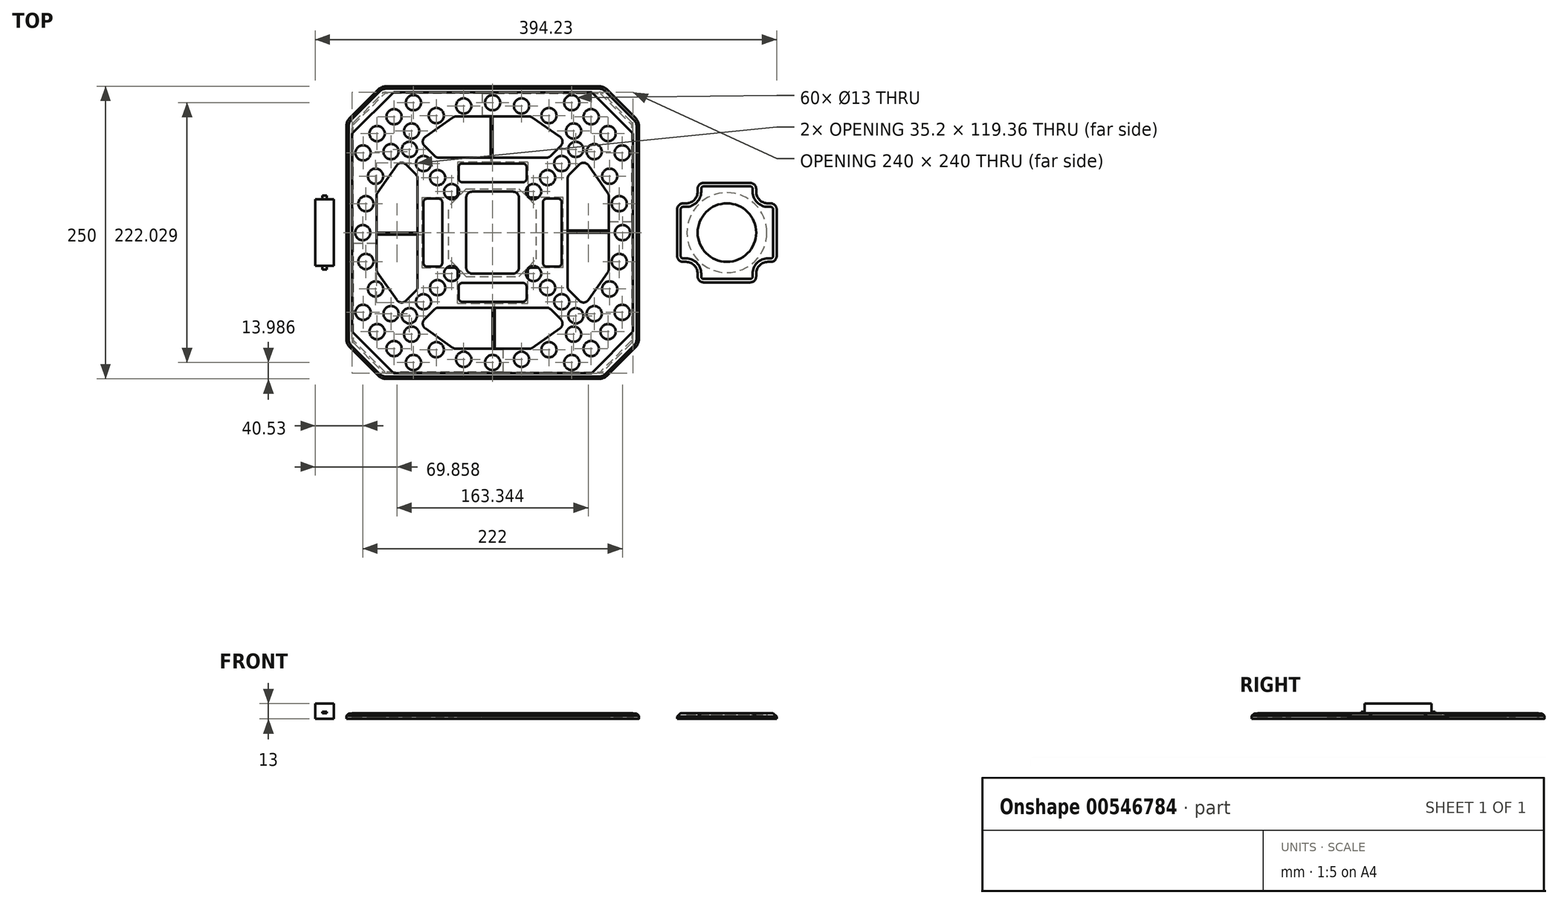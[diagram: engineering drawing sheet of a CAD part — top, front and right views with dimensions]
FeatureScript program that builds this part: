
annotation { "Feature Type Name" : "Feature", "Feature Type Description" : "" }
export const myFeature = defineFeature(function(context is Context, id is Id, definition is map)
    precondition{}
    {
        {
            var Q0;
            Q0=qCreatedBy(makeId("Top.planeOp"),FACE);
            var sketch = newSketch(context, id + "F0", { "sketchPlane" : qUnion([Q0])});
            skLineSegment(sketch, "E0.bottom", {"start": v(-90.86, 125) * mm, "end": v(90.86, 125) * mm});
            skLineSegment(sketch, "E0.top", {"start": v(-90.86, -125) * mm, "end": v(90.86, -125) * mm});
            skLineSegment(sketch, "E0.left", {"start": v(-125, 90.86) * mm, "end": v(-125, -90.86) * mm});
            skLineSegment(sketch, "E0.right", {"start": v(125, 90.86) * mm, "end": v(125, -90.86) * mm});
            skLineSegment(sketch, "E1", {"start": v(-183.74, 0) * mm, "end": v(184.86, 0) * mm, "construction": true});
            skLineSegment(sketch, "E2", {"start": v(0, -164.51) * mm, "end": v(0, 163.57) * mm, "construction": true});
            skLineSegment(sketch, "E3", {"start": v(-97.93, 122.07) * mm, "end": v(-122.07, 97.93) * mm});
            skLineSegment(sketch, "E4.MirrorCS", {"start": v(97.93, 122.07) * mm, "end": v(122.07, 97.93) * mm});
            skLineSegment(sketch, "E5.MirrorCS", {"start": v(97.93, -122.07) * mm, "end": v(122.07, -97.93) * mm});
            skLineSegment(sketch, "E6.MirrorCS", {"start": v(-97.93, -122.07) * mm, "end": v(-122.07, -97.93) * mm});
            skPoint(sketch, "E7.orphan", {"position": v(-125, 125) * mm});
            skPoint(sketch, "E8.0.visualSharp", {"position": v(-125, 95) * mm});
            skArc(sketch, "E8.0.filletArc", {"start": v(-122.07, 97.93) * mm, "mid": v(-124.24, 94.68) * mm, "end": v(-125, 90.86) * mm});
            skPoint(sketch, "E9.0.visualSharp", {"position": v(-95, 125) * mm});
            skArc(sketch, "E9.0.filletArc", {"start": v(-90.86, 125) * mm, "mid": v(-94.68, 124.24) * mm, "end": v(-97.93, 122.07) * mm});
            skPoint(sketch, "E9.1.visualSharp", {"position": v(95, 125) * mm});
            skArc(sketch, "E9.1.filletArc", {"start": v(97.93, 122.07) * mm, "mid": v(94.68, 124.24) * mm, "end": v(90.86, 125) * mm});
            skPoint(sketch, "E9.2.visualSharp", {"position": v(125, 95) * mm});
            skArc(sketch, "E9.2.filletArc", {"start": v(125, 90.86) * mm, "mid": v(124.24, 94.68) * mm, "end": v(122.07, 97.93) * mm});
            skPoint(sketch, "E9.3.visualSharp", {"position": v(125, -95) * mm});
            skArc(sketch, "E9.3.filletArc", {"start": v(122.07, -97.93) * mm, "mid": v(124.24, -94.68) * mm, "end": v(125, -90.86) * mm});
            skPoint(sketch, "E9.4.visualSharp", {"position": v(95, -125) * mm});
            skArc(sketch, "E9.4.filletArc", {"start": v(90.86, -125) * mm, "mid": v(94.68, -124.24) * mm, "end": v(97.93, -122.07) * mm});
            skPoint(sketch, "E9.5.visualSharp", {"position": v(-95, -125) * mm});
            skArc(sketch, "E9.5.filletArc", {"start": v(-97.93, -122.07) * mm, "mid": v(-94.68, -124.24) * mm, "end": v(-90.86, -125) * mm});
            skPoint(sketch, "E10.0.visualSharp", {"position": v(-125, -95) * mm});
            skArc(sketch, "E10.0.filletArc", {"start": v(-125, -90.86) * mm, "mid": v(-124.24, -94.68) * mm, "end": v(-122.07, -97.93) * mm});
            skSolve(sketch);
        }
        {
            var Q0;
            Q0 = qSketchRegion(id + "F0", true);
            extrude(context, id + "F1", {"entities" : qUnion([Q0]), "depth" : 5 * mm, "offsetDistance" : 25 * mm});
        }
        {
            var Q0;
            Q0=makeQuery(id+"F1.opExtrude","CAP_FACE",FACE,{"disambiguationData":[OSD([sQuery(id+"F0.wireOp",EDGE,"E0.bottom"),sQuery(id+"F0.wireOp",EDGE,"E0.top"),sQuery(id+"F0.wireOp",EDGE,"E0.left"),sQuery(id+"F0.wireOp",EDGE,"E0.right")])],"isStart":true});
            var sketch = newSketch(context, id + "F2", { "sketchPlane" : qUnion([Q0])});
            skLineSegment(sketch, "E11.bottom", {"start": v(-90.93, 120) * mm, "end": v(90.93, 120) * mm});
            skLineSegment(sketch, "E11.top", {"start": v(-90.93, -120) * mm, "end": v(90.93, -120) * mm});
            skLineSegment(sketch, "E11.left", {"start": v(-120, 90.93) * mm, "end": v(-120, -90.93) * mm});
            skLineSegment(sketch, "E11.right", {"start": v(120, 90.93) * mm, "end": v(120, -90.93) * mm});
            skLineSegment(sketch, "E12.bottom", {"start": v(-22.5, 37.5) * mm, "end": v(22.5, 37.5) * mm});
            skLineSegment(sketch, "E12.top", {"start": v(-22.5, -37.5) * mm, "end": v(22.5, -37.5) * mm});
            skLineSegment(sketch, "E12.left", {"start": v(-37.5, 22.5) * mm, "end": v(-37.5, -22.5) * mm});
            skLineSegment(sketch, "E12.right", {"start": v(37.5, 22.5) * mm, "end": v(37.5, -22.5) * mm});
            skLineSegment(sketch, "E13", {"start": v(-118.54, 94.46) * mm, "end": v(-94.46, 118.54) * mm});
            skLineSegment(sketch, "E14.MirrorCS", {"start": v(-118.54, -94.46) * mm, "end": v(-94.46, -118.54) * mm});
            skLineSegment(sketch, "E15.MirrorCS", {"start": v(120, -93) * mm, "end": v(93, -120) * mm});
            skLineSegment(sketch, "E16.MirrorCS", {"start": v(118.54, -94.46) * mm, "end": v(94.46, -118.54) * mm});
            skLineSegment(sketch, "E17.MirrorCS", {"start": v(118.54, 94.46) * mm, "end": v(94.46, 118.54) * mm});
            skPoint(sketch, "E18.orphan", {"position": v(-120, 120) * mm});
            skLineSegment(sketch, "E19", {"start": v(-22.5, -37.5) * mm, "end": v(-37.5, -22.5) * mm});
            skLineSegment(sketch, "E20.MirrorCS", {"start": v(22.5, -37.5) * mm, "end": v(37.5, -22.5) * mm});
            skLineSegment(sketch, "E21.MirrorCS", {"start": v(-22.5, 37.5) * mm, "end": v(-37.5, 22.5) * mm});
            skLineSegment(sketch, "E22.MirrorCS", {"start": v(22.5, 37.5) * mm, "end": v(37.5, 22.5) * mm});
            skPoint(sketch, "E23.orphan", {"position": v(-37.5, -37.5) * mm});
            skPoint(sketch, "E24.visualSharp", {"position": v(-120, 93) * mm});
            skArc(sketch, "E24.filletArc", {"start": v(-118.54, 94.46) * mm, "mid": v(-119.62, 92.84) * mm, "end": v(-120, 90.93) * mm});
            skPoint(sketch, "E25.visualSharp", {"position": v(-93, 120) * mm});
            skArc(sketch, "E25.filletArc", {"start": v(-90.93, 120) * mm, "mid": v(-92.84, 119.62) * mm, "end": v(-94.46, 118.54) * mm});
            skPoint(sketch, "E26.visualSharp", {"position": v(93, 120) * mm});
            skArc(sketch, "E26.filletArc", {"start": v(94.46, 118.54) * mm, "mid": v(92.84, 119.62) * mm, "end": v(90.93, 120) * mm});
            skPoint(sketch, "E27.visualSharp", {"position": v(120, 93) * mm});
            skArc(sketch, "E27.filletArc", {"start": v(120, 90.93) * mm, "mid": v(119.62, 92.84) * mm, "end": v(118.54, 94.46) * mm});
            skPoint(sketch, "E28.visualSharp", {"position": v(120, -93) * mm});
            skArc(sketch, "E28.filletArc", {"start": v(118.54, -94.46) * mm, "mid": v(119.62, -92.84) * mm, "end": v(120, -90.93) * mm});
            skPoint(sketch, "E29.visualSharp", {"position": v(93, -120) * mm});
            skArc(sketch, "E29.filletArc", {"start": v(90.93, -120) * mm, "mid": v(92.84, -119.62) * mm, "end": v(94.46, -118.54) * mm});
            skPoint(sketch, "E30.visualSharp", {"position": v(-93, -120) * mm});
            skArc(sketch, "E30.filletArc", {"start": v(-94.46, -118.54) * mm, "mid": v(-92.84, -119.62) * mm, "end": v(-90.93, -120) * mm});
            skPoint(sketch, "E31.visualSharp", {"position": v(-120, -93) * mm});
            skArc(sketch, "E31.filletArc", {"start": v(-120, -90.93) * mm, "mid": v(-119.62, -92.84) * mm, "end": v(-118.54, -94.46) * mm});
            skSolve(sketch);
        }
        {
            var Q0;
            Q0 = qSketchRegion(id + "F2", true);
            extrude(context, id + "F3", {"entities" : qUnion([Q0]), "operationType" : NewBodyOperationType.REMOVE, "oppositeDirection" : true, "depth" : 3 * mm, "offsetDistance" : 25 * mm});
        }
        {
            var Q0;
            Q0=makeQuery(id+"F1.opExtrude","CAP_FACE",FACE,{"disambiguationData":[OSD([sQuery(id+"F0.wireOp",EDGE,"E0.bottom"),sQuery(id+"F0.wireOp",EDGE,"E0.top"),sQuery(id+"F0.wireOp",EDGE,"E0.left"),sQuery(id+"F0.wireOp",EDGE,"E0.right")])],"isStart":false});
            var sketch = newSketch(context, id + "F4", { "sketchPlane" : qUnion([Q0])});
            skCircle(sketch, "E32", {"center": v(0, 111) * mm, "radius": 6.5 * mm});
            skCircle(sketch, "E33.1.0", {"center": v(24.7, 108.22) * mm, "radius": 6.5 * mm});
            skCircle(sketch, "E33.2.0", {"center": v(48.16, 100) * mm, "radius": 6.5 * mm});
            skCircle(sketch, "E33.3.0", {"center": v(69.2, 86.78) * mm, "radius": 6.5 * mm});
            skCircle(sketch, "E33.4.0", {"center": v(86.78, 69.2) * mm, "radius": 6.5 * mm});
            skCircle(sketch, "E33.5.0", {"center": v(100, 48.16) * mm, "radius": 6.5 * mm});
            skCircle(sketch, "E33.6.0", {"center": v(108.22, 24.7) * mm, "radius": 6.5 * mm});
            skCircle(sketch, "E33.7.0", {"center": v(111, 0) * mm, "radius": 6.5 * mm});
            skCircle(sketch, "E33.8.0", {"center": v(108.22, -24.7) * mm, "radius": 6.5 * mm});
            skCircle(sketch, "E33.9.0", {"center": v(100, -48.16) * mm, "radius": 6.5 * mm});
            skCircle(sketch, "E33.10.0", {"center": v(86.78, -69.2) * mm, "radius": 6.5 * mm});
            skCircle(sketch, "E33.11.0", {"center": v(69.2, -86.78) * mm, "radius": 6.5 * mm});
            skCircle(sketch, "E33.12.0", {"center": v(48.16, -100) * mm, "radius": 6.5 * mm});
            skCircle(sketch, "E33.13.0", {"center": v(24.7, -108.22) * mm, "radius": 6.5 * mm});
            skCircle(sketch, "E33.14.0", {"center": v(0, -111) * mm, "radius": 6.5 * mm});
            skCircle(sketch, "E33.15.0", {"center": v(-24.7, -108.22) * mm, "radius": 6.5 * mm});
            skCircle(sketch, "E33.16.0", {"center": v(-48.16, -100) * mm, "radius": 6.5 * mm});
            skCircle(sketch, "E33.17.0", {"center": v(-69.2, -86.78) * mm, "radius": 6.5 * mm});
            skCircle(sketch, "E33.18.0", {"center": v(-86.78, -69.2) * mm, "radius": 6.5 * mm});
            skCircle(sketch, "E33.19.0", {"center": v(-100, -48.16) * mm, "radius": 6.5 * mm});
            skCircle(sketch, "E33.20.0", {"center": v(-108.22, -24.7) * mm, "radius": 6.5 * mm});
            skCircle(sketch, "E33.21.0", {"center": v(-111, 0) * mm, "radius": 6.5 * mm});
            skCircle(sketch, "E33.22.0", {"center": v(-108.22, 24.7) * mm, "radius": 6.5 * mm});
            skCircle(sketch, "E33.23.0", {"center": v(-100, 48.16) * mm, "radius": 6.5 * mm});
            skCircle(sketch, "E33.24.0", {"center": v(-86.78, 69.2) * mm, "radius": 6.5 * mm});
            skCircle(sketch, "E33.25.0", {"center": v(-69.2, 86.78) * mm, "radius": 6.5 * mm});
            skCircle(sketch, "E33.26.0", {"center": v(-48.16, 100) * mm, "radius": 6.5 * mm});
            skCircle(sketch, "E33.27.0", {"center": v(-24.7, 108.22) * mm, "radius": 6.5 * mm});
            skLineSegment(sketch, "E33.anchor1", {"start": v(0, 0) * mm, "end": v(0, 111) * mm, "construction": true});
            skLineSegment(sketch, "E33.anchor2", {"start": v(0, 0) * mm, "end": v(-24.7, 108.22) * mm, "construction": true});
            skLineSegment(sketch, "E34.bottom", {"start": v(-17.5, 35) * mm, "end": v(17.5, 35) * mm});
            skLineSegment(sketch, "E34.top", {"start": v(-17.5, -35) * mm, "end": v(17.5, -35) * mm});
            skLineSegment(sketch, "E34.left", {"start": v(-22.5, 30) * mm, "end": v(-22.5, -30) * mm});
            skLineSegment(sketch, "E34.right", {"start": v(22.5, 30) * mm, "end": v(22.5, -30) * mm});
            skCircle(sketch, "E35", {"center": v(-110.72, 68.13) * mm, "radius": 6.5 * mm});
            skCircle(sketch, "E36.1.0", {"center": v(-98.68, 84.63) * mm, "radius": 6.5 * mm});
            skCircle(sketch, "E36.2.0", {"center": v(-84.2, 99.05) * mm, "radius": 6.5 * mm});
            skCircle(sketch, "E36.3.0", {"center": v(-67.64, 111.01) * mm, "radius": 6.5 * mm});
            skPoint(sketch, "E36.center", {"position": v(0, 0) * mm});
            skLineSegment(sketch, "E36.anchor1", {"start": v(0, 0) * mm, "end": v(-110.72, 68.13) * mm, "construction": true});
            skLineSegment(sketch, "E36.anchor2", {"start": v(0, 0) * mm, "end": v(-67.64, 111.01) * mm, "construction": true});
            skCircle(sketch, "E37.MirrorC", {"center": v(67.64, 111.01) * mm, "radius": 6.5 * mm});
            skCircle(sketch, "E38.MirrorC", {"center": v(84.2, 99.05) * mm, "radius": 6.5 * mm});
            skCircle(sketch, "E39.MirrorC", {"center": v(98.68, 84.63) * mm, "radius": 6.5 * mm});
            skCircle(sketch, "E40.MirrorC", {"center": v(110.72, 68.13) * mm, "radius": 6.5 * mm});
            skCircle(sketch, "E41.MirrorC", {"center": v(-110.72, -68.13) * mm, "radius": 6.5 * mm});
            skCircle(sketch, "E42.MirrorC", {"center": v(-98.68, -84.63) * mm, "radius": 6.5 * mm});
            skCircle(sketch, "E43.MirrorC", {"center": v(-84.2, -99.05) * mm, "radius": 6.5 * mm});
            skCircle(sketch, "E44.MirrorC", {"center": v(-67.64, -111.01) * mm, "radius": 6.5 * mm});
            skCircle(sketch, "E45.MirrorC", {"center": v(67.64, -111.01) * mm, "radius": 6.5 * mm});
            skCircle(sketch, "E46.MirrorC", {"center": v(84.2, -99.05) * mm, "radius": 6.5 * mm});
            skCircle(sketch, "E47.MirrorC", {"center": v(98.68, -84.63) * mm, "radius": 6.5 * mm});
            skCircle(sketch, "E48.MirrorC", {"center": v(110.72, -68.13) * mm, "radius": 6.5 * mm});
            skCircle(sketch, "E49", {"center": v(35, 35) * mm, "radius": 6.5 * mm});
            skCircle(sketch, "E50.1.0.0", {"center": v(47.02, 47.02) * mm, "radius": 6.5 * mm});
            skCircle(sketch, "E50.2.0.0", {"center": v(59.04, 59.04) * mm, "radius": 6.5 * mm});
            skCircle(sketch, "E50.3.0.0", {"center": v(71.06, 71.06) * mm, "radius": 6.5 * mm});
            skLineSegment(sketch, "E50.direction1", {"start": v(40, 40) * mm, "end": v(52.02, 52.02) * mm, "construction": true});
            skCircle(sketch, "E51.MirrorC", {"center": v(-71.06, 71.06) * mm, "radius": 6.5 * mm});
            skCircle(sketch, "E52.MirrorC", {"center": v(-59.04, 59.04) * mm, "radius": 6.5 * mm});
            skCircle(sketch, "E53.MirrorC", {"center": v(-47.02, 47.02) * mm, "radius": 6.5 * mm});
            skCircle(sketch, "E54.MirrorC", {"center": v(-35, 35) * mm, "radius": 6.5 * mm});
            skCircle(sketch, "E55.MirrorC", {"center": v(-71.06, -71.06) * mm, "radius": 6.5 * mm});
            skCircle(sketch, "E56.MirrorC", {"center": v(-59.04, -59.04) * mm, "radius": 6.5 * mm});
            skCircle(sketch, "E57.MirrorC", {"center": v(-47.02, -47.02) * mm, "radius": 6.5 * mm});
            skCircle(sketch, "E58.MirrorC", {"center": v(-35, -35) * mm, "radius": 6.5 * mm});
            skCircle(sketch, "E59.MirrorC", {"center": v(35, -35) * mm, "radius": 6.5 * mm});
            skCircle(sketch, "E60.MirrorC", {"center": v(47.02, -47.02) * mm, "radius": 6.5 * mm});
            skCircle(sketch, "E61.MirrorC", {"center": v(59.04, -59.04) * mm, "radius": 6.5 * mm});
            skCircle(sketch, "E62.MirrorC", {"center": v(71.06, -71.06) * mm, "radius": 6.5 * mm});
            skPoint(sketch, "E63.visualSharp", {"position": v(-22.5, 35) * mm});
            skArc(sketch, "E63.filletArc", {"start": v(-17.5, 35) * mm, "mid": v(-21.04, 33.54) * mm, "end": v(-22.5, 30) * mm});
            skPoint(sketch, "E64.visualSharp", {"position": v(22.5, 35) * mm});
            skArc(sketch, "E64.filletArc", {"start": v(22.5, 30) * mm, "mid": v(21.04, 33.54) * mm, "end": v(17.5, 35) * mm});
            skPoint(sketch, "E65.visualSharp", {"position": v(22.5, -35) * mm});
            skArc(sketch, "E65.filletArc", {"start": v(17.5, -35) * mm, "mid": v(21.04, -33.54) * mm, "end": v(22.5, -30) * mm});
            skPoint(sketch, "E66.visualSharp", {"position": v(-22.5, -35) * mm});
            skArc(sketch, "E66.filletArc", {"start": v(-22.5, -30) * mm, "mid": v(-21.04, -33.54) * mm, "end": v(-17.5, -35) * mm});
            skLineSegment(sketch, "E67.bottom", {"start": v(-46.04, 29) * mm, "end": v(-56.04, 29) * mm});
            skLineSegment(sketch, "E67.top", {"start": v(-46.04, -29) * mm, "end": v(-56.04, -29) * mm});
            skLineSegment(sketch, "E67.left", {"start": v(-43.04, 26) * mm, "end": v(-43.04, -26) * mm});
            skLineSegment(sketch, "E67.right", {"start": v(-59.04, 26) * mm, "end": v(-59.04, -26) * mm});
            skPoint(sketch, "E68.visualSharp", {"position": v(-43.04, -29) * mm});
            skArc(sketch, "E68.filletArc", {"start": v(-46.04, -29) * mm, "mid": v(-43.92, -28.12) * mm, "end": v(-43.04, -26) * mm});
            skPoint(sketch, "E69.visualSharp", {"position": v(-59.04, -29) * mm});
            skArc(sketch, "E69.filletArc", {"start": v(-59.04, -26) * mm, "mid": v(-58.16, -28.12) * mm, "end": v(-56.04, -29) * mm});
            skPoint(sketch, "E70.visualSharp", {"position": v(-59.04, 29) * mm});
            skArc(sketch, "E70.filletArc", {"start": v(-56.04, 29) * mm, "mid": v(-58.16, 28.12) * mm, "end": v(-59.04, 26) * mm});
            skPoint(sketch, "E71.visualSharp", {"position": v(-43.04, 29) * mm});
            skArc(sketch, "E71.filletArc", {"start": v(-43.04, 26) * mm, "mid": v(-43.92, 28.12) * mm, "end": v(-46.04, 29) * mm});
            skPoint(sketch, "E72.1.0", {"position": v(-29, -59.04) * mm});
            skPoint(sketch, "E72.1.1", {"position": v(-29, -43.04) * mm});
            skLineSegment(sketch, "E72.1.2", {"start": v(-29, -46.04) * mm, "end": v(-29, -56.04) * mm});
            skLineSegment(sketch, "E72.1.3", {"start": v(29, -46.04) * mm, "end": v(29, -56.04) * mm});
            skPoint(sketch, "E72.1.4", {"position": v(29, -43.04) * mm});
            skLineSegment(sketch, "E72.1.5", {"start": v(-26, -59.04) * mm, "end": v(26, -59.04) * mm});
            skPoint(sketch, "E72.1.6", {"position": v(29, -59.04) * mm});
            skLineSegment(sketch, "E72.1.7", {"start": v(-26, -43.04) * mm, "end": v(26, -43.04) * mm});
            skArc(sketch, "E72.1.8", {"start": v(26, -59.04) * mm, "mid": v(28.12, -58.16) * mm, "end": v(29, -56.04) * mm});
            skArc(sketch, "E72.1.9", {"start": v(-26, -43.04) * mm, "mid": v(-28.12, -43.92) * mm, "end": v(-29, -46.04) * mm});
            skArc(sketch, "E72.1.10", {"start": v(29, -46.04) * mm, "mid": v(28.12, -43.92) * mm, "end": v(26, -43.04) * mm});
            skArc(sketch, "E72.1.11", {"start": v(-29, -56.04) * mm, "mid": v(-28.12, -58.16) * mm, "end": v(-26, -59.04) * mm});
            skPoint(sketch, "E72.2.0", {"position": v(59.04, -29) * mm});
            skPoint(sketch, "E72.2.1", {"position": v(43.04, -29) * mm});
            skLineSegment(sketch, "E72.2.2", {"start": v(46.04, -29) * mm, "end": v(56.04, -29) * mm});
            skLineSegment(sketch, "E72.2.3", {"start": v(46.04, 29) * mm, "end": v(56.04, 29) * mm});
            skPoint(sketch, "E72.2.4", {"position": v(43.04, 29) * mm});
            skLineSegment(sketch, "E72.2.5", {"start": v(59.04, -26) * mm, "end": v(59.04, 26) * mm});
            skPoint(sketch, "E72.2.6", {"position": v(59.04, 29) * mm});
            skLineSegment(sketch, "E72.2.7", {"start": v(43.04, -26) * mm, "end": v(43.04, 26) * mm});
            skArc(sketch, "E72.2.8", {"start": v(59.04, 26) * mm, "mid": v(58.16, 28.12) * mm, "end": v(56.04, 29) * mm});
            skArc(sketch, "E72.2.9", {"start": v(43.04, -26) * mm, "mid": v(43.92, -28.12) * mm, "end": v(46.04, -29) * mm});
            skArc(sketch, "E72.2.10", {"start": v(46.04, 29) * mm, "mid": v(43.92, 28.12) * mm, "end": v(43.04, 26) * mm});
            skArc(sketch, "E72.2.11", {"start": v(56.04, -29) * mm, "mid": v(58.16, -28.12) * mm, "end": v(59.04, -26) * mm});
            skPoint(sketch, "E72.3.0", {"position": v(29, 59.04) * mm});
            skPoint(sketch, "E72.3.1", {"position": v(29, 43.04) * mm});
            skLineSegment(sketch, "E72.3.2", {"start": v(29, 46.04) * mm, "end": v(29, 56.04) * mm});
            skLineSegment(sketch, "E72.3.3", {"start": v(-29, 46.04) * mm, "end": v(-29, 56.04) * mm});
            skPoint(sketch, "E72.3.4", {"position": v(-29, 43.04) * mm});
            skLineSegment(sketch, "E72.3.5", {"start": v(26, 59.04) * mm, "end": v(-26, 59.04) * mm});
            skPoint(sketch, "E72.3.6", {"position": v(-29, 59.04) * mm});
            skLineSegment(sketch, "E72.3.7", {"start": v(26, 43.04) * mm, "end": v(-26, 43.04) * mm});
            skArc(sketch, "E72.3.8", {"start": v(-26, 59.04) * mm, "mid": v(-28.12, 58.16) * mm, "end": v(-29, 56.04) * mm});
            skArc(sketch, "E72.3.9", {"start": v(26, 43.04) * mm, "mid": v(28.12, 43.92) * mm, "end": v(29, 46.04) * mm});
            skArc(sketch, "E72.3.10", {"start": v(-29, 46.04) * mm, "mid": v(-28.12, 43.92) * mm, "end": v(-26, 43.04) * mm});
            skArc(sketch, "E72.3.11", {"start": v(29, 56.04) * mm, "mid": v(28.12, 58.16) * mm, "end": v(26, 59.04) * mm});
            skLineSegment(sketch, "E73", {"start": v(-70.1, 0) * mm, "end": v(72.67, 0) * mm, "construction": true});
            skLineSegment(sketch, "E74", {"start": v(0, -68) * mm, "end": v(0, 72.3) * mm, "construction": true});
            skSolve(sketch);
        }
        {
            var Q0;
            Q0 = qSketchRegion(id + "F4", true);
            extrude(context, id + "F5", {"entities" : qUnion([Q0]), "operationType" : NewBodyOperationType.REMOVE, "oppositeDirection" : true, "depth" : 4 * mm, "offsetDistance" : 25 * mm});
        }
        {
            var Q0;
            Q0=qCreatedBy(makeId("Top.planeOp"),FACE);
            var sketch = newSketch(context, id + "F6", { "sketchPlane" : qUnion([Q0])});
            skLineSegment(sketch, "E75.bottom", {"start": v(165.2, 25) * mm, "end": v(162.7, 25) * mm});
            skLineSegment(sketch, "E75.top", {"start": v(237.7, -25) * mm, "end": v(235.2, -25) * mm});
            skLineSegment(sketch, "E75.left", {"start": v(242.7, 20) * mm, "end": v(242.7, -20) * mm});
            skLineSegment(sketch, "E75.right", {"start": v(157.7, 20) * mm, "end": v(157.7, -20) * mm});
            skPoint(sketch, "E75.middle", {"position": v(200.2, 0) * mm});
            skLineSegment(sketch, "E76.bottom", {"start": v(220.2, 42.5) * mm, "end": v(180.2, 42.5) * mm});
            skLineSegment(sketch, "E76.top", {"start": v(220.2, -42.5) * mm, "end": v(180.2, -42.5) * mm});
            skLineSegment(sketch, "E76.left", {"start": v(225.2, 37.5) * mm, "end": v(225.2, 35) * mm});
            skLineSegment(sketch, "E76.right", {"start": v(175.2, 37.5) * mm, "end": v(175.2, 35) * mm});
            skPoint(sketch, "E77.newPointB", {"position": v(242.7, 25) * mm});
            skArc(sketch, "E77.filletArc", {"start": v(165.2, 25) * mm, "mid": v(172.27, 27.93) * mm, "end": v(175.2, 35) * mm});
            skArc(sketch, "E78.MirrorCS", {"start": v(235.2, 25) * mm, "mid": v(228.13, 27.93) * mm, "end": v(225.2, 35) * mm});
            skArc(sketch, "E79.MirrorCS", {"start": v(165.2, -25) * mm, "mid": v(172.27, -27.93) * mm, "end": v(175.2, -35) * mm});
            skArc(sketch, "E80.MirrorCS", {"start": v(235.2, -25) * mm, "mid": v(228.13, -27.93) * mm, "end": v(225.2, -35) * mm});
            skLineSegment(sketch, "E81", {"start": v(175.2, -35) * mm, "end": v(175.2, -37.5) * mm});
            skLineSegment(sketch, "E82", {"start": v(235.2, 25) * mm, "end": v(237.7, 25) * mm});
            skLineSegment(sketch, "E83.trimOffspring", {"start": v(225.2, -35) * mm, "end": v(225.2, -37.5) * mm});
            skLineSegment(sketch, "E84.trimOffspring", {"start": v(165.2, -25) * mm, "end": v(162.7, -25) * mm});
            skPoint(sketch, "E85.visualSharp", {"position": v(157.7, 25) * mm});
            skArc(sketch, "E85.filletArc", {"start": v(162.7, 25) * mm, "mid": v(159.16, 23.54) * mm, "end": v(157.7, 20) * mm});
            skPoint(sketch, "E86.visualSharp", {"position": v(157.7, -25) * mm});
            skArc(sketch, "E86.filletArc", {"start": v(157.7, -20) * mm, "mid": v(159.16, -23.54) * mm, "end": v(162.7, -25) * mm});
            skPoint(sketch, "E87.visualSharp", {"position": v(175.2, 42.5) * mm});
            skArc(sketch, "E87.filletArc", {"start": v(180.2, 42.5) * mm, "mid": v(176.66, 41.04) * mm, "end": v(175.2, 37.5) * mm});
            skPoint(sketch, "E88.visualSharp", {"position": v(225.2, 42.5) * mm});
            skArc(sketch, "E88.filletArc", {"start": v(225.2, 37.5) * mm, "mid": v(223.74, 41.04) * mm, "end": v(220.2, 42.5) * mm});
            skArc(sketch, "E89.filletArc", {"start": v(242.7, 20) * mm, "mid": v(241.24, 23.54) * mm, "end": v(237.7, 25) * mm});
            skPoint(sketch, "E90.visualSharp", {"position": v(242.7, -25) * mm});
            skArc(sketch, "E90.filletArc", {"start": v(237.7, -25) * mm, "mid": v(241.24, -23.54) * mm, "end": v(242.7, -20) * mm});
            skPoint(sketch, "E91.visualSharp", {"position": v(225.2, -42.5) * mm});
            skArc(sketch, "E91.filletArc", {"start": v(220.2, -42.5) * mm, "mid": v(223.74, -41.04) * mm, "end": v(225.2, -37.5) * mm});
            skPoint(sketch, "E92.visualSharp", {"position": v(175.2, -42.5) * mm});
            skArc(sketch, "E92.filletArc", {"start": v(175.2, -37.5) * mm, "mid": v(176.66, -41.04) * mm, "end": v(180.2, -42.5) * mm});
            skCircle(sketch, "E93", {"center": v(200.2, 0) * mm, "radius": 25 * mm});
            skSolve(sketch);
        }
        {
            var Q0;
            Q0 = qSketchRegion(id + "F6", true);
            extrude(context, id + "F7", {"entities" : qUnion([Q0]), "depth" : 5 * mm, "offsetDistance" : 25 * mm});
        }
        {
            var Q0;
            Q0=makeQuery(id+"F1.opExtrude","CAP_FACE",FACE,{"disambiguationData":[OSD([sQuery(id+"F0.wireOp",EDGE,"E0.bottom"),sQuery(id+"F0.wireOp",EDGE,"E0.top"),sQuery(id+"F0.wireOp",EDGE,"E0.left"),sQuery(id+"F0.wireOp",EDGE,"E0.right"),sQuery(id+"F0.wireOp",EDGE,"E3"),sQuery(id+"F0.wireOp",EDGE,"E4.MirrorCS"),sQuery(id+"F0.wireOp",EDGE,"E5.MirrorCS"),sQuery(id+"F0.wireOp",EDGE,"0a14f579-07f0-4295-ad88-e3387aad065c0.MirrorCS")])],"isStart":false});
            var sketch = newSketch(context, id + "F8", { "sketchPlane" : qUnion([Q0])});
            skSolve(sketch);
        }
        {
            var Q0;
            Q0=makeQuery(id+"F8.imprint","IMPRINT",FACE,{"disambiguationData":[TD([[makeQuery(id+"F8.imprint","IMPRINT",EDGE,{"derivedFrom":makeQuery(id+"F1.opExtrude","CAP_EDGE",EDGE,{"disambiguationData":[OSD([sQuery(id+"F0.wireOp",EDGE,"E0.bottom")])],"isStart":false})}),-1.0]])]});
            var sketch = newSketch(context, id + "F9", { "sketchPlane" : qUnion([Q0])});
            skLineSegment(sketch, "E94", {"start": v(0, 64.07) * mm, "end": v(46.1, 64.07) * mm});
            skLineSegment(sketch, "E95", {"start": v(49.63, 65.54) * mm, "end": v(58.23, 74.14) * mm});
            skLineSegment(sketch, "E96.MirrorCS", {"start": v(0, 64.07) * mm, "end": v(-46.1, 64.07) * mm});
            skLineSegment(sketch, "E97.MirrorCS", {"start": v(-49.63, 65.54) * mm, "end": v(-58.23, 74.14) * mm});
            skLineSegment(sketch, "E98.1.0", {"start": v(-65.54, -49.63) * mm, "end": v(-74.14, -58.23) * mm});
            skLineSegment(sketch, "E98.1.1", {"start": v(-64.07, 0) * mm, "end": v(-64.07, -46.1) * mm});
            skLineSegment(sketch, "E98.1.2", {"start": v(-64.07, 0) * mm, "end": v(-64.07, 46.1) * mm});
            skLineSegment(sketch, "E98.1.3", {"start": v(-65.54, 49.63) * mm, "end": v(-74.14, 58.23) * mm});
            skLineSegment(sketch, "E98.2.0", {"start": v(49.63, -65.54) * mm, "end": v(58.23, -74.14) * mm});
            skLineSegment(sketch, "E98.2.1", {"start": v(0, -64.07) * mm, "end": v(46.1, -64.07) * mm});
            skLineSegment(sketch, "E98.2.2", {"start": v(0, -64.07) * mm, "end": v(-46.1, -64.07) * mm});
            skLineSegment(sketch, "E98.2.3", {"start": v(-49.63, -65.54) * mm, "end": v(-58.23, -74.14) * mm});
            skLineSegment(sketch, "E98.3.0", {"start": v(65.54, 49.63) * mm, "end": v(74.14, 58.23) * mm});
            skLineSegment(sketch, "E98.3.1", {"start": v(64.07, 0) * mm, "end": v(64.07, 46.1) * mm});
            skLineSegment(sketch, "E98.3.2", {"start": v(64.07, 0) * mm, "end": v(64.07, -46.1) * mm});
            skLineSegment(sketch, "E98.3.3", {"start": v(65.54, -49.63) * mm, "end": v(74.14, -58.23) * mm});
            skPoint(sketch, "E98.center", {"position": v(0, 0) * mm});
            skPoint(sketch, "E99.visualSharp", {"position": v(-78.22, 62.3) * mm});
            skArc(sketch, "E99.filletArc", {"start": v(-74.14, 58.23) * mm, "mid": v(-78.1, 59.68) * mm, "end": v(-81.76, 57.58) * mm});
            skPoint(sketch, "E100.visualSharp", {"position": v(-64.07, 48.17) * mm});
            skArc(sketch, "E100.filletArc", {"start": v(-64.07, 46.1) * mm, "mid": v(-64.45, 48) * mm, "end": v(-65.54, 49.63) * mm});
            skPoint(sketch, "E101.visualSharp", {"position": v(-64.07, -48.17) * mm});
            skArc(sketch, "E101.filletArc", {"start": v(-65.54, -49.63) * mm, "mid": v(-64.45, -48) * mm, "end": v(-64.07, -46.1) * mm});
            skPoint(sketch, "E102.visualSharp", {"position": v(-78.22, -62.3) * mm});
            skArc(sketch, "E102.filletArc", {"start": v(-81.76, -57.58) * mm, "mid": v(-78.1, -59.68) * mm, "end": v(-74.14, -58.23) * mm});
            skPoint(sketch, "E103.visualSharp", {"position": v(-62.3, 78.22) * mm});
            skArc(sketch, "E103.filletArc", {"start": v(-57.58, 81.76) * mm, "mid": v(-59.68, 78.1) * mm, "end": v(-58.23, 74.14) * mm});
            skPoint(sketch, "E104.visualSharp", {"position": v(-48.17, 64.07) * mm});
            skArc(sketch, "E104.filletArc", {"start": v(-49.63, 65.54) * mm, "mid": v(-48, 64.45) * mm, "end": v(-46.1, 64.07) * mm});
            skPoint(sketch, "E105.visualSharp", {"position": v(48.17, 64.07) * mm});
            skArc(sketch, "E105.filletArc", {"start": v(46.1, 64.07) * mm, "mid": v(48, 64.45) * mm, "end": v(49.63, 65.54) * mm});
            skPoint(sketch, "E106.visualSharp", {"position": v(62.3, 78.22) * mm});
            skArc(sketch, "E106.filletArc", {"start": v(58.23, 74.14) * mm, "mid": v(59.68, 78.1) * mm, "end": v(57.58, 81.76) * mm});
            skPoint(sketch, "E107.visualSharp", {"position": v(78.22, 62.3) * mm});
            skArc(sketch, "E107.filletArc", {"start": v(81.76, 57.58) * mm, "mid": v(78.1, 59.68) * mm, "end": v(74.14, 58.23) * mm});
            skPoint(sketch, "E108.visualSharp", {"position": v(64.07, 48.17) * mm});
            skArc(sketch, "E108.filletArc", {"start": v(65.54, 49.63) * mm, "mid": v(64.45, 48) * mm, "end": v(64.07, 46.1) * mm});
            skPoint(sketch, "E109.visualSharp", {"position": v(64.07, -48.17) * mm});
            skArc(sketch, "E109.filletArc", {"start": v(64.07, -46.1) * mm, "mid": v(64.45, -48) * mm, "end": v(65.54, -49.63) * mm});
            skPoint(sketch, "E110.visualSharp", {"position": v(78.22, -62.3) * mm});
            skArc(sketch, "E110.filletArc", {"start": v(74.14, -58.23) * mm, "mid": v(78.1, -59.68) * mm, "end": v(81.76, -57.58) * mm});
            skPoint(sketch, "E111.visualSharp", {"position": v(48.17, -64.07) * mm});
            skArc(sketch, "E111.filletArc", {"start": v(49.63, -65.54) * mm, "mid": v(48, -64.45) * mm, "end": v(46.1, -64.07) * mm});
            skPoint(sketch, "E112.visualSharp", {"position": v(62.3, -78.22) * mm});
            skArc(sketch, "E112.filletArc", {"start": v(57.58, -81.76) * mm, "mid": v(59.68, -78.1) * mm, "end": v(58.23, -74.14) * mm});
            skPoint(sketch, "E113.visualSharp", {"position": v(-62.3, -78.22) * mm});
            skArc(sketch, "E113.filletArc", {"start": v(-58.23, -74.14) * mm, "mid": v(-59.68, -78.1) * mm, "end": v(-57.58, -81.76) * mm});
            skPoint(sketch, "E114.visualSharp", {"position": v(-48.17, -64.07) * mm});
            skArc(sketch, "E114.filletArc", {"start": v(-46.1, -64.07) * mm, "mid": v(-48, -64.45) * mm, "end": v(-49.63, -65.54) * mm});
            skLineSegment(sketch, "E115", {"start": v(-57.58, 81.76) * mm, "end": v(-34, 98.36) * mm});
            skLineSegment(sketch, "E116.MirrorCS", {"start": v(57.58, 81.76) * mm, "end": v(34, 98.36) * mm});
            skLineSegment(sketch, "E117.1.0", {"start": v(-81.76, -57.58) * mm, "end": v(-98.36, -34) * mm});
            skLineSegment(sketch, "E117.1.3", {"start": v(-81.76, 57.58) * mm, "end": v(-98.36, 34) * mm});
            skLineSegment(sketch, "E117.2.0", {"start": v(57.58, -81.76) * mm, "end": v(34, -98.36) * mm});
            skLineSegment(sketch, "E117.2.3", {"start": v(-57.58, -81.76) * mm, "end": v(-34, -98.36) * mm});
            skLineSegment(sketch, "E117.3.0", {"start": v(81.76, 57.58) * mm, "end": v(98.36, 34) * mm});
            skLineSegment(sketch, "E117.3.3", {"start": v(81.76, -57.58) * mm, "end": v(98.36, -34) * mm});
            skLineSegment(sketch, "E118", {"start": v(-99.27, 31.13) * mm, "end": v(-99.27, -31.13) * mm});
            skLineSegment(sketch, "E119", {"start": v(-31.13, 99.27) * mm, "end": v(31.13, 99.27) * mm});
            skLineSegment(sketch, "E120", {"start": v(99.27, 31.13) * mm, "end": v(99.27, -31.13) * mm});
            skLineSegment(sketch, "E121", {"start": v(-31.13, -99.27) * mm, "end": v(31.13, -99.27) * mm});
            skPoint(sketch, "E122.MirrorCS.end.orphan", {"position": v(0, 100.03) * mm});
            skPoint(sketch, "E122.MirrorCS.start.orphan", {"position": v(32.71, 99.27) * mm});
            skPoint(sketch, "E123.0.visualSharp", {"position": v(-99.27, 32.71) * mm});
            skArc(sketch, "E123.0.filletArc", {"start": v(-98.36, 34) * mm, "mid": v(-99.04, 32.64) * mm, "end": v(-99.27, 31.13) * mm});
            skPoint(sketch, "E123.1.visualSharp", {"position": v(-99.27, -32.71) * mm});
            skArc(sketch, "E123.1.filletArc", {"start": v(-99.27, -31.13) * mm, "mid": v(-99.04, -32.64) * mm, "end": v(-98.36, -34) * mm});
            skPoint(sketch, "E123.2.visualSharp", {"position": v(-32.71, 99.27) * mm});
            skArc(sketch, "E123.2.filletArc", {"start": v(-31.13, 99.27) * mm, "mid": v(-32.64, 99.04) * mm, "end": v(-34, 98.36) * mm});
            skArc(sketch, "E123.3.filletArc", {"start": v(34, 98.36) * mm, "mid": v(32.64, 99.04) * mm, "end": v(31.13, 99.27) * mm});
            skPoint(sketch, "E123.4.visualSharp", {"position": v(99.27, 32.71) * mm});
            skArc(sketch, "E123.4.filletArc", {"start": v(99.27, 31.13) * mm, "mid": v(99.04, 32.64) * mm, "end": v(98.36, 34) * mm});
            skPoint(sketch, "E123.5.visualSharp", {"position": v(99.27, -32.71) * mm});
            skArc(sketch, "E123.5.filletArc", {"start": v(98.36, -34) * mm, "mid": v(99.04, -32.64) * mm, "end": v(99.27, -31.13) * mm});
            skPoint(sketch, "E123.6.visualSharp", {"position": v(32.71, -99.27) * mm});
            skArc(sketch, "E123.6.filletArc", {"start": v(31.13, -99.27) * mm, "mid": v(32.64, -99.04) * mm, "end": v(34, -98.36) * mm});
            skPoint(sketch, "E123.7.visualSharp", {"position": v(-32.71, -99.27) * mm});
            skArc(sketch, "E123.7.filletArc", {"start": v(-34, -98.36) * mm, "mid": v(-32.64, -99.04) * mm, "end": v(-31.13, -99.27) * mm});
            skSolve(sketch);
        }
        {
            var Q0;
            Q0 = qSketchRegion(id + "F9", true);
            extrude(context, id + "F10", {"entities" : qUnion([Q0]), "operationType" : NewBodyOperationType.REMOVE, "oppositeDirection" : true, "depth" : 2 * mm, "offsetDistance" : 25 * mm});
        }
        {
            var Q0;
            Q0=makeQuery(id+"F8.imprint","IMPRINT",FACE,{"disambiguationData":[TD([[makeQuery(id+"F8.imprint","IMPRINT",EDGE,{"derivedFrom":makeQuery(id+"F1.opExtrude","CAP_EDGE",EDGE,{"disambiguationData":[OSD([sQuery(id+"F0.wireOp",EDGE,"E0.bottom")])],"isStart":false})}),-1.0]])]});
            var sketch = newSketch(context, id + "F11", { "sketchPlane" : qUnion([Q0])});
            skLineSegment(sketch, "E124.bottom", {"start": v(-150, 150) * mm, "end": v(150, 150) * mm});
            skLineSegment(sketch, "E124.top", {"start": v(-150, -150) * mm, "end": v(150, -150) * mm});
            skLineSegment(sketch, "E124.left", {"start": v(-150, 150) * mm, "end": v(-150, -150) * mm});
            skLineSegment(sketch, "E124.right", {"start": v(150, 150) * mm, "end": v(150, -150) * mm});
            skLineSegment(sketch, "E125", {"start": v(-150, 150) * mm, "end": v(150, -150) * mm, "construction": true});
            skLineSegment(sketch, "E126", {"start": v(-150, -150) * mm, "end": v(150, 150) * mm, "construction": true});
            skLineSegment(sketch, "E127", {"start": v(-102.32, -102.32) * mm, "end": v(-120, -84.64) * mm});
            skLineSegment(sketch, "E128", {"start": v(-120, -84.64) * mm, "end": v(-120, 84.64) * mm});
            skLineSegment(sketch, "E129.MirrorCS", {"start": v(-102.32, 102.32) * mm, "end": v(-120, 84.64) * mm});
            skLineSegment(sketch, "E130.MirrorCS", {"start": v(-102.32, 102.32) * mm, "end": v(-84.64, 120) * mm});
            skLineSegment(sketch, "E131.MirrorCS", {"start": v(84.64, 120) * mm, "end": v(-84.64, 120) * mm});
            skLineSegment(sketch, "E132.MirrorCS", {"start": v(102.32, 102.32) * mm, "end": v(84.64, 120) * mm});
            skLineSegment(sketch, "E133.MirrorCS", {"start": v(102.32, 102.32) * mm, "end": v(120, 84.64) * mm});
            skLineSegment(sketch, "E134.MirrorCS", {"start": v(120, 84.64) * mm, "end": v(120, -84.64) * mm});
            skLineSegment(sketch, "E135.MirrorCS", {"start": v(102.32, -102.32) * mm, "end": v(120, -84.64) * mm});
            skLineSegment(sketch, "E136.MirrorCS", {"start": v(102.32, -102.32) * mm, "end": v(84.64, -120) * mm});
            skLineSegment(sketch, "E137.MirrorCS", {"start": v(-84.64, -120) * mm, "end": v(84.64, -120) * mm});
            skLineSegment(sketch, "E138.MirrorCS", {"start": v(-102.32, -102.32) * mm, "end": v(-84.64, -120) * mm});
            skSolve(sketch);
        }
        {
            var Q0;
            Q0 = qSketchRegion(id + "F11", true);
            extrude(context, id + "F12", {"entities" : qUnion([Q0]), "operationType" : NewBodyOperationType.REMOVE, "oppositeDirection" : true, "depth" : 0.5 * mm, "offsetDistance" : 25 * mm});
        }
        {
            var Q0;
            Q0=makeQuery(id+"F7.opExtrude","CAP_FACE",FACE,{"disambiguationData":[OSD([sQuery(id+"F6.wireOp",EDGE,"E75.bottom"),sQuery(id+"F6.wireOp",EDGE,"E75.top"),sQuery(id+"F6.wireOp",EDGE,"E75.left"),sQuery(id+"F6.wireOp",EDGE,"E75.right"),sQuery(id+"F6.wireOp",EDGE,"E76.bottom"),sQuery(id+"F6.wireOp",EDGE,"E76.top"),sQuery(id+"F6.wireOp",EDGE,"E76.left"),sQuery(id+"F6.wireOp",EDGE,"E76.right"),sQuery(id+"F6.wireOp",EDGE,"E77.filletArc"),sQuery(id+"F6.wireOp",EDGE,"E78.MirrorCS"),sQuery(id+"F6.wireOp",EDGE,"E79.MirrorCS"),sQuery(id+"F6.wireOp",EDGE,"E80.MirrorCS"),sQuery(id+"F6.wireOp",EDGE,"E81"),sQuery(id+"F6.wireOp",EDGE,"E82"),sQuery(id+"F6.wireOp",EDGE,"E83.trimOffspring"),sQuery(id+"F6.wireOp",EDGE,"E84.trimOffspring"),sQuery(id+"F6.wireOp",EDGE,"E85.filletArc"),sQuery(id+"F6.wireOp",EDGE,"E86.filletArc"),sQuery(id+"F6.wireOp",EDGE,"E87.filletArc"),sQuery(id+"F6.wireOp",EDGE,"E88.filletArc"),sQuery(id+"F6.wireOp",EDGE,"E89.filletArc"),sQuery(id+"F6.wireOp",EDGE,"E90.filletArc"),sQuery(id+"F6.wireOp",EDGE,"E91.filletArc"),sQuery(id+"F6.wireOp",EDGE,"E92.filletArc"),sQuery(id+"F6.wireOp",EDGE,"E93")])],"isStart":true});
            var sketch = newSketch(context, id + "F13", { "sketchPlane" : qUnion([Q0])});
            skCircle(sketch, "E139", {"center": v(200.2, 0) * mm, "radius": 34.18 * mm});
            skSolve(sketch);
        }
        {
            var Q0;
            Q0 = qSketchRegion(id + "F13", true);
            extrude(context, id + "F14", {"entities" : qUnion([Q0]), "operationType" : NewBodyOperationType.REMOVE, "oppositeDirection" : true, "depth" : 4 * mm, "offsetDistance" : 25 * mm});
        }
        {
            var Q0;
            Q0=makeQuery(id+"F12.boolean.opBoolean","INTERSECT",EDGE,{"derivedFrom":[makeQuery(id+"F1.opExtrude","SWEPT_FACE",FACE,{"disambiguationData":[OSD([sQuery(id+"F0.wireOp",EDGE,"0a14f579-07f0-4295-ad88-e3387aad065c0.MirrorCS")])]}),makeQuery(id+"F12.opExtrude","CAP_FACE",FACE,{"disambiguationData":[OSD([sQuery(id+"F11.wireOp",EDGE,"E124.bottom"),sQuery(id+"F11.wireOp",EDGE,"E124.top"),sQuery(id+"F11.wireOp",EDGE,"E124.left"),sQuery(id+"F11.wireOp",EDGE,"E124.right"),sQuery(id+"F11.wireOp",EDGE,"E127"),sQuery(id+"F11.wireOp",EDGE,"E128"),sQuery(id+"F11.wireOp",EDGE,"E129.MirrorCS"),sQuery(id+"F11.wireOp",EDGE,"E130.MirrorCS"),sQuery(id+"F11.wireOp",EDGE,"E131.MirrorCS"),sQuery(id+"F11.wireOp",EDGE,"E132.MirrorCS"),sQuery(id+"F11.wireOp",EDGE,"E133.MirrorCS"),sQuery(id+"F11.wireOp",EDGE,"E134.MirrorCS"),sQuery(id+"F11.wireOp",EDGE,"E135.MirrorCS"),sQuery(id+"F11.wireOp",EDGE,"E136.MirrorCS"),sQuery(id+"F11.wireOp",EDGE,"E137.MirrorCS"),sQuery(id+"F11.wireOp",EDGE,"E138.MirrorCS")])],"isStart":false})]});
            var Q1;
            Q1=makeQuery(id+"F12.boolean.opBoolean","INTERSECT",EDGE,{"derivedFrom":[makeQuery(id+"F1.opExtrude","SWEPT_FACE",FACE,{"disambiguationData":[OSD([sQuery(id+"F0.wireOp",EDGE,"E0.top")])]}),makeQuery(id+"F12.opExtrude","CAP_FACE",FACE,{"disambiguationData":[OSD([sQuery(id+"F11.wireOp",EDGE,"E124.bottom"),sQuery(id+"F11.wireOp",EDGE,"E124.top"),sQuery(id+"F11.wireOp",EDGE,"E124.left"),sQuery(id+"F11.wireOp",EDGE,"E124.right"),sQuery(id+"F11.wireOp",EDGE,"E127"),sQuery(id+"F11.wireOp",EDGE,"E128"),sQuery(id+"F11.wireOp",EDGE,"E129.MirrorCS"),sQuery(id+"F11.wireOp",EDGE,"E130.MirrorCS"),sQuery(id+"F11.wireOp",EDGE,"E131.MirrorCS"),sQuery(id+"F11.wireOp",EDGE,"E132.MirrorCS"),sQuery(id+"F11.wireOp",EDGE,"E133.MirrorCS"),sQuery(id+"F11.wireOp",EDGE,"E134.MirrorCS"),sQuery(id+"F11.wireOp",EDGE,"E135.MirrorCS"),sQuery(id+"F11.wireOp",EDGE,"E136.MirrorCS"),sQuery(id+"F11.wireOp",EDGE,"E137.MirrorCS"),sQuery(id+"F11.wireOp",EDGE,"E138.MirrorCS")])],"isStart":false})]});
            var Q2;
            Q2=makeQuery(id+"F12.boolean.opBoolean","INTERSECT",EDGE,{"derivedFrom":[makeQuery(id+"F1.opExtrude","SWEPT_FACE",FACE,{"disambiguationData":[OSD([sQuery(id+"F0.wireOp",EDGE,"E5.MirrorCS")])]}),makeQuery(id+"F12.opExtrude","CAP_FACE",FACE,{"disambiguationData":[OSD([sQuery(id+"F11.wireOp",EDGE,"E124.bottom"),sQuery(id+"F11.wireOp",EDGE,"E124.top"),sQuery(id+"F11.wireOp",EDGE,"E124.left"),sQuery(id+"F11.wireOp",EDGE,"E124.right"),sQuery(id+"F11.wireOp",EDGE,"E127"),sQuery(id+"F11.wireOp",EDGE,"E128"),sQuery(id+"F11.wireOp",EDGE,"E129.MirrorCS"),sQuery(id+"F11.wireOp",EDGE,"E130.MirrorCS"),sQuery(id+"F11.wireOp",EDGE,"E131.MirrorCS"),sQuery(id+"F11.wireOp",EDGE,"E132.MirrorCS"),sQuery(id+"F11.wireOp",EDGE,"E133.MirrorCS"),sQuery(id+"F11.wireOp",EDGE,"E134.MirrorCS"),sQuery(id+"F11.wireOp",EDGE,"E135.MirrorCS"),sQuery(id+"F11.wireOp",EDGE,"E136.MirrorCS"),sQuery(id+"F11.wireOp",EDGE,"E137.MirrorCS"),sQuery(id+"F11.wireOp",EDGE,"E138.MirrorCS")])],"isStart":false})]});
            var Q3;
            Q3=makeQuery(id+"F12.boolean.opBoolean","INTERSECT",EDGE,{"derivedFrom":[makeQuery(id+"F1.opExtrude","SWEPT_FACE",FACE,{"disambiguationData":[OSD([sQuery(id+"F0.wireOp",EDGE,"E0.right")])]}),makeQuery(id+"F12.opExtrude","CAP_FACE",FACE,{"disambiguationData":[OSD([sQuery(id+"F11.wireOp",EDGE,"E124.bottom"),sQuery(id+"F11.wireOp",EDGE,"E124.top"),sQuery(id+"F11.wireOp",EDGE,"E124.left"),sQuery(id+"F11.wireOp",EDGE,"E124.right"),sQuery(id+"F11.wireOp",EDGE,"E127"),sQuery(id+"F11.wireOp",EDGE,"E128"),sQuery(id+"F11.wireOp",EDGE,"E129.MirrorCS"),sQuery(id+"F11.wireOp",EDGE,"E130.MirrorCS"),sQuery(id+"F11.wireOp",EDGE,"E131.MirrorCS"),sQuery(id+"F11.wireOp",EDGE,"E132.MirrorCS"),sQuery(id+"F11.wireOp",EDGE,"E133.MirrorCS"),sQuery(id+"F11.wireOp",EDGE,"E134.MirrorCS"),sQuery(id+"F11.wireOp",EDGE,"E135.MirrorCS"),sQuery(id+"F11.wireOp",EDGE,"E136.MirrorCS"),sQuery(id+"F11.wireOp",EDGE,"E137.MirrorCS"),sQuery(id+"F11.wireOp",EDGE,"E138.MirrorCS")])],"isStart":false})]});
            var Q4;
            Q4=makeQuery(id+"F12.boolean.opBoolean","INTERSECT",EDGE,{"derivedFrom":[makeQuery(id+"F1.opExtrude","SWEPT_FACE",FACE,{"disambiguationData":[OSD([sQuery(id+"F0.wireOp",EDGE,"E0.left")])]}),makeQuery(id+"F12.opExtrude","CAP_FACE",FACE,{"disambiguationData":[OSD([sQuery(id+"F11.wireOp",EDGE,"E124.bottom"),sQuery(id+"F11.wireOp",EDGE,"E124.top"),sQuery(id+"F11.wireOp",EDGE,"E124.left"),sQuery(id+"F11.wireOp",EDGE,"E124.right"),sQuery(id+"F11.wireOp",EDGE,"E127"),sQuery(id+"F11.wireOp",EDGE,"E128"),sQuery(id+"F11.wireOp",EDGE,"E129.MirrorCS"),sQuery(id+"F11.wireOp",EDGE,"E130.MirrorCS"),sQuery(id+"F11.wireOp",EDGE,"E131.MirrorCS"),sQuery(id+"F11.wireOp",EDGE,"E132.MirrorCS"),sQuery(id+"F11.wireOp",EDGE,"E133.MirrorCS"),sQuery(id+"F11.wireOp",EDGE,"E134.MirrorCS"),sQuery(id+"F11.wireOp",EDGE,"E135.MirrorCS"),sQuery(id+"F11.wireOp",EDGE,"E136.MirrorCS"),sQuery(id+"F11.wireOp",EDGE,"E137.MirrorCS"),sQuery(id+"F11.wireOp",EDGE,"E138.MirrorCS")])],"isStart":false})]});
            var Q5;
            Q5=makeQuery(id+"F12.boolean.opBoolean","INTERSECT",EDGE,{"derivedFrom":[makeQuery(id+"F1.opExtrude","SWEPT_FACE",FACE,{"disambiguationData":[OSD([sQuery(id+"F0.wireOp",EDGE,"E4.MirrorCS")])]}),makeQuery(id+"F12.opExtrude","CAP_FACE",FACE,{"disambiguationData":[OSD([sQuery(id+"F11.wireOp",EDGE,"E124.bottom"),sQuery(id+"F11.wireOp",EDGE,"E124.top"),sQuery(id+"F11.wireOp",EDGE,"E124.left"),sQuery(id+"F11.wireOp",EDGE,"E124.right"),sQuery(id+"F11.wireOp",EDGE,"E127"),sQuery(id+"F11.wireOp",EDGE,"E128"),sQuery(id+"F11.wireOp",EDGE,"E129.MirrorCS"),sQuery(id+"F11.wireOp",EDGE,"E130.MirrorCS"),sQuery(id+"F11.wireOp",EDGE,"E131.MirrorCS"),sQuery(id+"F11.wireOp",EDGE,"E132.MirrorCS"),sQuery(id+"F11.wireOp",EDGE,"E133.MirrorCS"),sQuery(id+"F11.wireOp",EDGE,"E134.MirrorCS"),sQuery(id+"F11.wireOp",EDGE,"E135.MirrorCS"),sQuery(id+"F11.wireOp",EDGE,"E136.MirrorCS"),sQuery(id+"F11.wireOp",EDGE,"E137.MirrorCS"),sQuery(id+"F11.wireOp",EDGE,"E138.MirrorCS")])],"isStart":false})]});
            var Q6;
            Q6=makeQuery(id+"F12.boolean.opBoolean","INTERSECT",EDGE,{"derivedFrom":[makeQuery(id+"F1.opExtrude","SWEPT_FACE",FACE,{"disambiguationData":[OSD([sQuery(id+"F0.wireOp",EDGE,"E0.bottom")])]}),makeQuery(id+"F12.opExtrude","CAP_FACE",FACE,{"disambiguationData":[OSD([sQuery(id+"F11.wireOp",EDGE,"E124.bottom"),sQuery(id+"F11.wireOp",EDGE,"E124.top"),sQuery(id+"F11.wireOp",EDGE,"E124.left"),sQuery(id+"F11.wireOp",EDGE,"E124.right"),sQuery(id+"F11.wireOp",EDGE,"E127"),sQuery(id+"F11.wireOp",EDGE,"E128"),sQuery(id+"F11.wireOp",EDGE,"E129.MirrorCS"),sQuery(id+"F11.wireOp",EDGE,"E130.MirrorCS"),sQuery(id+"F11.wireOp",EDGE,"E131.MirrorCS"),sQuery(id+"F11.wireOp",EDGE,"E132.MirrorCS"),sQuery(id+"F11.wireOp",EDGE,"E133.MirrorCS"),sQuery(id+"F11.wireOp",EDGE,"E134.MirrorCS"),sQuery(id+"F11.wireOp",EDGE,"E135.MirrorCS"),sQuery(id+"F11.wireOp",EDGE,"E136.MirrorCS"),sQuery(id+"F11.wireOp",EDGE,"E137.MirrorCS"),sQuery(id+"F11.wireOp",EDGE,"E138.MirrorCS")])],"isStart":false})]});
            var Q7;
            Q7=makeQuery(id+"F12.boolean.opBoolean","INTERSECT",EDGE,{"derivedFrom":[makeQuery(id+"F1.opExtrude","SWEPT_FACE",FACE,{"disambiguationData":[OSD([sQuery(id+"F0.wireOp",EDGE,"E3")])]}),makeQuery(id+"F12.opExtrude","CAP_FACE",FACE,{"disambiguationData":[OSD([sQuery(id+"F11.wireOp",EDGE,"E124.bottom"),sQuery(id+"F11.wireOp",EDGE,"E124.top"),sQuery(id+"F11.wireOp",EDGE,"E124.left"),sQuery(id+"F11.wireOp",EDGE,"E124.right"),sQuery(id+"F11.wireOp",EDGE,"E127"),sQuery(id+"F11.wireOp",EDGE,"E128"),sQuery(id+"F11.wireOp",EDGE,"E129.MirrorCS"),sQuery(id+"F11.wireOp",EDGE,"E130.MirrorCS"),sQuery(id+"F11.wireOp",EDGE,"E131.MirrorCS"),sQuery(id+"F11.wireOp",EDGE,"E132.MirrorCS"),sQuery(id+"F11.wireOp",EDGE,"E133.MirrorCS"),sQuery(id+"F11.wireOp",EDGE,"E134.MirrorCS"),sQuery(id+"F11.wireOp",EDGE,"E135.MirrorCS"),sQuery(id+"F11.wireOp",EDGE,"E136.MirrorCS"),sQuery(id+"F11.wireOp",EDGE,"E137.MirrorCS"),sQuery(id+"F11.wireOp",EDGE,"E138.MirrorCS")])],"isStart":false})]});
            chamfer(context, id + "F15", {"entities" : qUnion([Q0, Q1, Q2, Q3, Q4, Q5, Q6, Q7]), "width" : 2 * mm, "tangentPropagation" : true});
        }
        {
            var Q0;
            Q0=makeQuery(id+"F7.opExtrude","CAP_EDGE",EDGE,{"disambiguationData":[OSD([sQuery(id+"F6.wireOp",EDGE,"E75.right")])],"isStart":false});
            chamfer(context, id + "F16", {"entities" : qUnion([Q0]), "width" : 3 * mm, "tangentPropagation" : true});
        }
        {
            var Q0;
            Q0=qCreatedBy(makeId("Top.planeOp"),FACE);
            var sketch = newSketch(context, id + "F17", { "sketchPlane" : qUnion([Q0])});
            skLineSegment(sketch, "E140", {"start": v(0, 0) * mm, "end": v(-158.96, 0) * mm, "construction": true});
            skLineSegment(sketch, "E141.bottom", {"start": v(-135.53, 28.5) * mm, "end": v(-151.53, 28.5) * mm});
            skLineSegment(sketch, "E141.top", {"start": v(-135.53, -28.5) * mm, "end": v(-151.53, -28.5) * mm});
            skLineSegment(sketch, "E141.left", {"start": v(-135.53, 28.5) * mm, "end": v(-135.53, -28.5) * mm});
            skLineSegment(sketch, "E141.right", {"start": v(-151.53, 28.5) * mm, "end": v(-151.53, -28.5) * mm});
            skPoint(sketch, "E141.middle", {"position": v(-143.53, 0) * mm});
            skSolve(sketch);
        }
        {
            var Q0;
            Q0 = qSketchRegion(id + "F17", true);
            extrude(context, id + "F18", {"entities" : qUnion([Q0]), "depth" : 13 * mm, "offsetDistance" : 25 * mm});
        }
        {
            var Q0;
            Q0=qCreatedBy(makeId("Top.planeOp"),FACE);
            var sketch = newSketch(context, id + "F19", { "sketchPlane" : qUnion([Q0])});
            skLineSegment(sketch, "E142.bottom", {"start": v(-141.62, 31.63) * mm, "end": v(-145.44, 31.63) * mm});
            skLineSegment(sketch, "E142.top", {"start": v(-141.62, -31.37) * mm, "end": v(-145.44, -31.37) * mm});
            skLineSegment(sketch, "E142.left", {"start": v(-141.62, 31.63) * mm, "end": v(-141.62, -31.37) * mm});
            skLineSegment(sketch, "E142.right", {"start": v(-145.44, 31.63) * mm, "end": v(-145.44, -31.37) * mm});
            skSolve(sketch);
        }
        {
            var Q0;
            Q0 = qSketchRegion(id + "F19", true);
            extrude(context, id + "F20", {"entities" : qUnion([Q0]), "operationType" : NewBodyOperationType.ADD, "depth" : 6 * mm, "offsetDistance" : 25 * mm, "hasSecondDirection" : true, "secondDirectionOppositeDirection" : false, "secondDirectionDepth" : 5 * mm});
        }
        {
            var Q0;
            Q0=qCreatedBy(makeId("Top.planeOp"),FACE);
            var sketch = newSketch(context, id + "F21", { "sketchPlane" : qUnion([Q0])});
            skLineSegment(sketch, "E143.right", {"start": v(-119, -9.03) * mm, "end": v(-119, 92) * mm});
            skPoint(sketch, "E143.middle", {"position": v(0, 0) * mm});
            skLineSegment(sketch, "E144", {"start": v(0, -134.65) * mm, "end": v(0, 60.27) * mm, "construction": true});
            skLineSegment(sketch, "E145", {"start": v(0, 0) * mm, "end": v(-119, 119) * mm, "construction": true});
            skLineSegment(sketch, "E146", {"start": v(-60.27, 9.03) * mm, "end": v(-60.27, 30) * mm});
            skLineSegment(sketch, "E147", {"start": v(-60.27, 30) * mm, "end": v(-33, 30) * mm});
            skLineSegment(sketch, "E148.MirrorCS", {"start": v(-30, 60.27) * mm, "end": v(-30, 33) * mm});
            skLineSegment(sketch, "E149.MirrorCS", {"start": v(-119, 92) * mm, "end": v(-92, 119) * mm});
            skPoint(sketch, "E150.visualSharp", {"position": v(-30, 30) * mm});
            skArc(sketch, "E150.filletArc", {"start": v(-33, 30) * mm, "mid": v(-30.88, 30.88) * mm, "end": v(-30, 33) * mm});
            skLineSegment(sketch, "E151", {"start": v(-119, -9.03) * mm, "end": v(-99.78, -9.03) * mm});
            skLineSegment(sketch, "E152.MirrorCS", {"start": v(-9.03, 119) * mm, "end": v(-9.03, 99.78) * mm});
            skLineSegment(sketch, "E153.trimOffspring", {"start": v(-9.03, 60.27) * mm, "end": v(-30, 60.27) * mm});
            skLineSegment(sketch, "E154.trimOffspring", {"start": v(-9.03, 119) * mm, "end": v(-92, 119) * mm});
            skLineSegment(sketch, "E155", {"start": v(-9.03, 60.27) * mm, "end": v(-1.66, 60.27) * mm});
            skLineSegment(sketch, "E156", {"start": v(-1.66, 99.78) * mm, "end": v(-9.03, 99.78) * mm});
            skLineSegment(sketch, "E157.MirrorCS", {"start": v(-60.27, 9.03) * mm, "end": v(-60.27, 0) * mm});
            skLineSegment(sketch, "E158.MirrorCS", {"start": v(-60.27, 0) * mm, "end": v(-99.78, 0) * mm});
            skLineSegment(sketch, "E159", {"start": v(-99.78, 0) * mm, "end": v(-99.78, -9.03) * mm});
            skLineSegment(sketch, "E160", {"start": v(-1.66, 99.78) * mm, "end": v(-1.66, 60.27) * mm});
            skLineSegment(sketch, "E161.trimOffspring", {"start": v(0, 99.78) * mm, "end": v(0, 142.8) * mm, "construction": true});
            skSolve(sketch);
        }
        {
            var Q0;
            Q0 = qSketchRegion(id + "F21", true);
            extrude(context, id + "F22", {"entities" : qUnion([Q0]), "depth" : 2 * mm, "offsetDistance" : 25 * mm});
        }
        {
            var Q0;
            Q0=qCreatedBy(makeId("Front.planeOp"),FACE);
            var sketch = newSketch(context, id + "F23", { "sketchPlane" : qUnion([Q0])});
            skLineSegment(sketch, "E162", {"start": v(0, -83.26) * mm, "end": v(0, 89.9) * mm});
            skSolve(sketch);
        }
        {
            var Q0;
            Q0=makeQuery(id+"F22.opExtrude","SWEPT_BODY",BODY,{"disambiguationData":[OSD([sQuery(id+"F21.wireOp",EDGE,"E143.right"),sQuery(id+"F21.wireOp",EDGE,"E146"),sQuery(id+"F21.wireOp",EDGE,"E147"),sQuery(id+"F21.wireOp",EDGE,"E148.MirrorCS"),sQuery(id+"F21.wireOp",EDGE,"E149.MirrorCS"),sQuery(id+"F21.wireOp",EDGE,"E150.filletArc"),sQuery(id+"F21.wireOp",EDGE,"E151"),sQuery(id+"F21.wireOp",EDGE,"E152.MirrorCS"),sQuery(id+"F21.wireOp",EDGE,"E153.trimOffspring"),sQuery(id+"F21.wireOp",EDGE,"E154.trimOffspring")])]});
            var Q1;
            Q1=sQuery(id+"F23.wireOp",EDGE,"E162");
            transform(context, id + "F24", {"entities" : qUnion([Q0]), "transformType" : TransformType.ROTATION, "transformAxis" : qUnion([Q1]), "angle" : 90 * degree, "makeCopy" : true});
        }
        {
            var Q0;
            Q0=makeQuery(id+"F22.opExtrude","SWEPT_BODY",BODY,{"disambiguationData":[OSD([sQuery(id+"F21.wireOp",EDGE,"E143.right"),sQuery(id+"F21.wireOp",EDGE,"E146"),sQuery(id+"F21.wireOp",EDGE,"E147"),sQuery(id+"F21.wireOp",EDGE,"E148.MirrorCS"),sQuery(id+"F21.wireOp",EDGE,"E149.MirrorCS"),sQuery(id+"F21.wireOp",EDGE,"E150.filletArc"),sQuery(id+"F21.wireOp",EDGE,"E151"),sQuery(id+"F21.wireOp",EDGE,"E152.MirrorCS"),sQuery(id+"F21.wireOp",EDGE,"E153.trimOffspring"),sQuery(id+"F21.wireOp",EDGE,"E154.trimOffspring")])]});
            var Q1;
            Q1=sQuery(id+"F23.wireOp",EDGE,"E162");
            transform(context, id + "F25", {"entities" : qUnion([Q0]), "transformType" : TransformType.ROTATION, "transformAxis" : qUnion([Q1]), "angle" : 180 * degree, "makeCopy" : true});
        }
        {
            var Q0;
            Q0=makeQuery(id+"F22.opExtrude","SWEPT_BODY",BODY,{"disambiguationData":[OSD([sQuery(id+"F21.wireOp",EDGE,"E143.right"),sQuery(id+"F21.wireOp",EDGE,"E146"),sQuery(id+"F21.wireOp",EDGE,"E147"),sQuery(id+"F21.wireOp",EDGE,"E148.MirrorCS"),sQuery(id+"F21.wireOp",EDGE,"E149.MirrorCS"),sQuery(id+"F21.wireOp",EDGE,"E150.filletArc"),sQuery(id+"F21.wireOp",EDGE,"E151"),sQuery(id+"F21.wireOp",EDGE,"E152.MirrorCS"),sQuery(id+"F21.wireOp",EDGE,"E153.trimOffspring"),sQuery(id+"F21.wireOp",EDGE,"E154.trimOffspring")])]});
            var Q1;
            Q1=sQuery(id+"F23.wireOp",EDGE,"E162");
            transform(context, id + "F26", {"entities" : qUnion([Q0]), "transformType" : TransformType.ROTATION, "transformAxis" : qUnion([Q1]), "angle" : 270 * degree, "makeCopy" : true});
        }
    });
